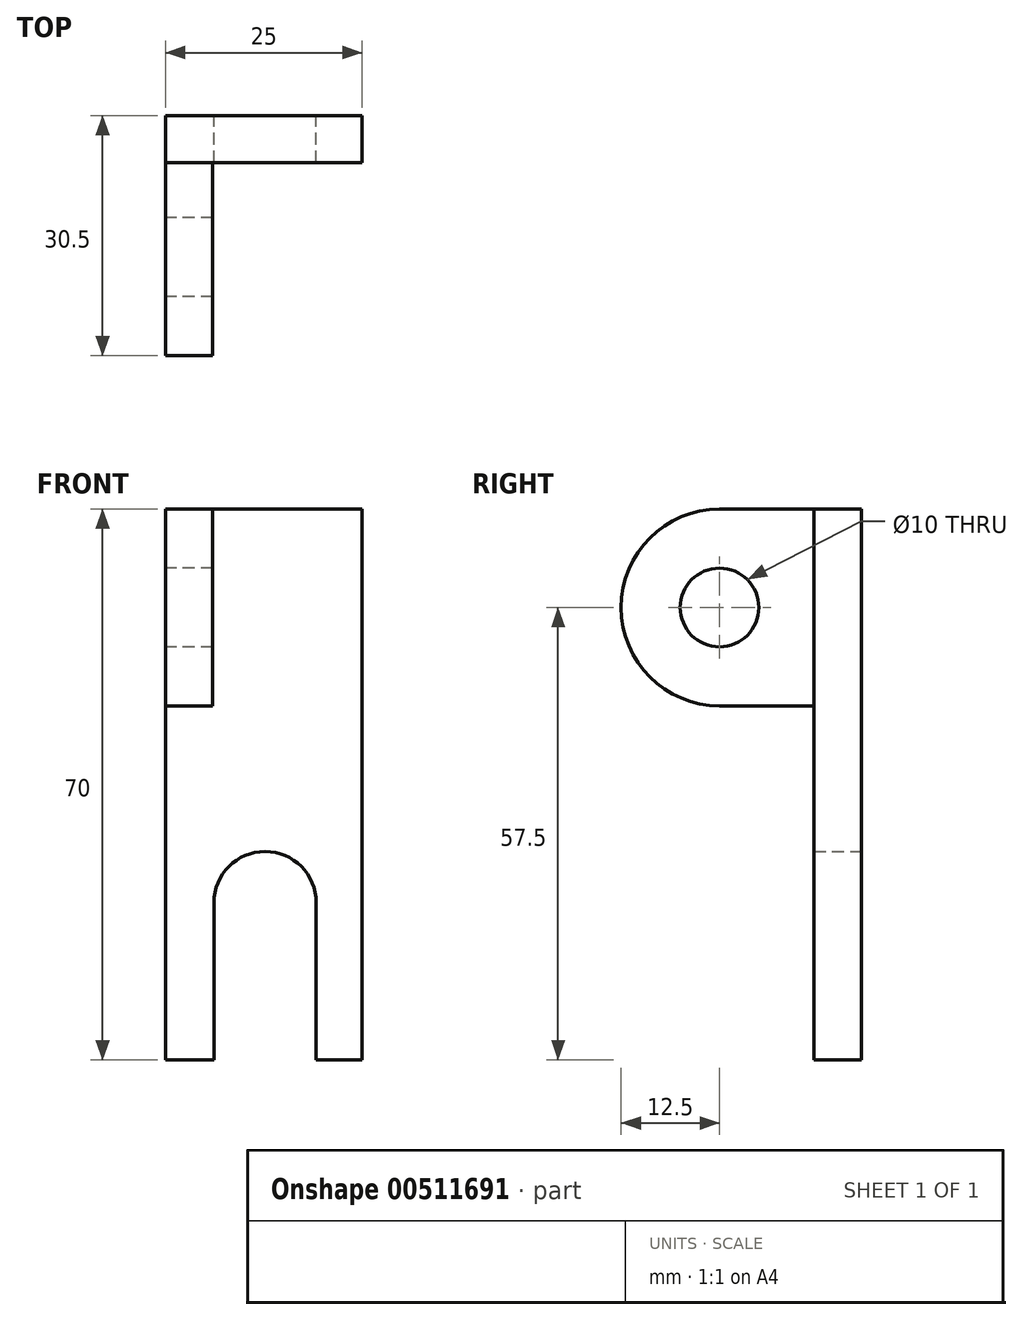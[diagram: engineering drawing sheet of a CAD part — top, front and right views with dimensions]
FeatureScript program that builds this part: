
annotation { "Feature Type Name" : "Feature", "Feature Type Description" : "" }
export const myFeature = defineFeature(function(context is Context, id is Id, definition is map)
    precondition{}
    {
        {
            var Q0;
            Q0=qCreatedBy(makeId("Front.planeOp"),FACE);
            var sketch = newSketch(context, id + "F0", { "sketchPlane" : qUnion([Q0])});
            skLineSegment(sketch, "E0.bottom", {"start": v(-12.5, 32) * mm, "end": v(12.5, 32) * mm});
            skLineSegment(sketch, "E0.top", {"start": v(-12.5, -32) * mm, "end": v(12.5, -32) * mm});
            skLineSegment(sketch, "E0.left", {"start": v(-12.5, 32) * mm, "end": v(-12.5, -32) * mm});
            skLineSegment(sketch, "E0.right", {"start": v(12.5, 32) * mm, "end": v(12.5, -32) * mm});
            skPoint(sketch, "E0.middle", {"position": v(0, 0) * mm});
            skSolve(sketch);
        }
        {
            var Q0;
            Q0 = qSketchRegion(id + "F0", true);
            extrude(context, id + "F1", {"entities" : qUnion([Q0]), "depth" : 6 * mm, "offsetDistance" : 25.4 * mm});
        }
        {
            var Q0;
            Q0=makeQuery(id+"F1.opExtrude","SWEPT_FACE",FACE,{"disambiguationData":[OSD([sQuery(id+"F0.wireOp",EDGE,"E0.bottom")])]});
            var sketch = newSketch(context, id + "F2", { "sketchPlane" : qUnion([Q0])});
            skLineSegment(sketch, "E1", {"start": v(-12.5, -6) * mm, "end": v(-12.5, 12) * mm});
            skLineSegment(sketch, "E2", {"start": v(12.5, -6) * mm, "end": v(12.5, 12) * mm});
            skArc(sketch, "E3", {"start": v(-12.5, 12) * mm, "mid": v(0, 24.5) * mm, "end": v(12.5, 12) * mm});
            skSolve(sketch);
        }
        {
            var Q0;
            {var subQ2=sQuery(id+"F2.wireOp",EDGE,"E3");Q0=makeQuery(id+"F2.imprint","IMPRINT",FACE,{"disambiguationData":[TD([[makeQuery(id+"F2.imprint","IMPRINT",EDGE,{"derivedFrom":subQ2}),-1.0]])]});}
            var Q1;
            {var subQ1=sQuery(id+"F0.wireOp",EDGE,"E0.bottom");var subQ2=makeQuery(id+"F1.opExtrude","CAP_EDGE",EDGE,{"disambiguationData":[OSD([subQ1])],"isStart":true});Q1=makeQuery(id+"F2.imprint","IMPRINT",FACE,{"disambiguationData":[TD([[makeQuery(id+"F2.imprint","IMPRINT",EDGE,{"derivedFrom":subQ2}),-1.0]])]});}
            extrude(context, id + "F3", {"entities" : qUnion([Q0, Q1]), "operationType" : NewBodyOperationType.ADD, "depth" : 6 * mm, "offsetDistance" : 25.4 * mm});
        }
        {
            var Q0;
            Q0=makeQuery(id+"F3.boolean.opBoolean","MERGE",FACE,{"derivedFrom":[makeQuery(id+"F1.opExtrude","SWEPT_FACE",FACE,{"disambiguationData":[OSD([sQuery(id+"F0.wireOp",EDGE,"E0.left")])]}),makeQuery(id+"F3.opExtrude","SWEPT_FACE",FACE,{"disambiguationData":[OSD([sQuery(id+"F2.wireOp",EDGE,"E1")])]})]});
            var sketch = newSketch(context, id + "F4", { "sketchPlane" : qUnion([Q0])});
            skPoint(sketch, "E4", {"position": v(0, 38) * mm});
            skPoint(sketch, "E5", {"position": v(0, 13) * mm});
            skLineSegment(sketch, "E6", {"start": v(0, 13) * mm, "end": v(18, 13) * mm});
            skLineSegment(sketch, "E7", {"start": v(0, 38) * mm, "end": v(18, 38) * mm});
            skArc(sketch, "E8", {"start": v(18, 13) * mm, "mid": v(30.5, 25.5) * mm, "end": v(18, 38) * mm});
            skSolve(sketch);
        }
        {
            var Q0;
            {var subQ0=sQuery(id+"F4.wireOp",EDGE,"E8");Q0=makeQuery(id+"F4.imprint","IMPRINT",FACE,{"disambiguationData":[TD([[makeQuery(id+"F4.imprint","IMPRINT",EDGE,{"derivedFrom":subQ0}),1.0]])]});}
            extrude(context, id + "F5", {"entities" : qUnion([Q0]), "oppositeDirection" : true, "depth" : 6 * mm, "offsetDistance" : 25.4 * mm});
        }
        {
            var Q0;
            Q0=makeQuery(id+"F3.opExtrude","CAP_FACE",FACE,{"disambiguationData":[OSD([sQuery(id+"F0.wireOp",EDGE,"E0.bottom"),sQuery(id+"F2.wireOp",EDGE,"E1"),sQuery(id+"F2.wireOp",EDGE,"E2"),sQuery(id+"F2.wireOp",EDGE,"E3")])],"isStart":false});
            var sketch = newSketch(context, id + "F6", { "sketchPlane" : qUnion([Q0])});
            skPoint(sketch, "E9", {"position": v(0, 12) * mm});
            skSolve(sketch);
        }
        {
            var Q0;
            Q0=sQuery(id+"F6.wireOp",VERTEX,"E9");
            var Q1;
            Q1=makeQuery(id+"F1.opExtrude","SWEPT_BODY",BODY,{"disambiguationData":[OSD([sQuery(id+"F0.wireOp",EDGE,"E0.bottom"),sQuery(id+"F0.wireOp",EDGE,"E0.top"),sQuery(id+"F0.wireOp",EDGE,"E0.left"),sQuery(id+"F0.wireOp",EDGE,"E0.right")])]});
            hole(context, id + "F7", {"style" : HoleStyle.SIMPLE, "endStyle" : HoleEndStyle.BLIND, "holeDiameter" : 10 * mm, "majorDiameter" : 6.35 * mm, "holeDepth" : 13 * mm, "isTappedThrough" : true, "tappedDepth" : 12.7 * mm, "tapClearance" : 3, "locations" : qUnion([Q0]), "scope" : qUnion([Q1])});
        }
        {
            var Q0;
            Q0=makeQuery(id+"F5.opExtrude","CAP_FACE",FACE,{"disambiguationData":[OSD([sQuery(id+"F0.wireOp",EDGE,"E0.bottom"),sQuery(id+"F0.wireOp",EDGE,"E0.left"),sQuery(id+"F2.wireOp",EDGE,"E1"),sQuery(id+"F4.wireOp",EDGE,"E6"),sQuery(id+"F4.wireOp",EDGE,"E7"),sQuery(id+"F4.wireOp",EDGE,"E8")])],"isStart":true});
            var sketch = newSketch(context, id + "F8", { "sketchPlane" : qUnion([Q0])});
            skPoint(sketch, "E10", {"position": v(18, 25.5) * mm});
            skSolve(sketch);
        }
        {
            var Q0;
            Q0=sQuery(id+"F8.wireOp",VERTEX,"E10");
            var Q1;
            Q1=makeQuery(id+"F5.opExtrude","SWEPT_BODY",BODY,{"disambiguationData":[OSD([sQuery(id+"F0.wireOp",EDGE,"E0.bottom"),sQuery(id+"F0.wireOp",EDGE,"E0.left"),sQuery(id+"F2.wireOp",EDGE,"E1"),sQuery(id+"F4.wireOp",EDGE,"E6"),sQuery(id+"F4.wireOp",EDGE,"E7"),sQuery(id+"F4.wireOp",EDGE,"E8")])]});
            hole(context, id + "F9", {"style" : HoleStyle.SIMPLE, "endStyle" : HoleEndStyle.BLIND, "holeDiameter" : 10 * mm, "majorDiameter" : 6.35 * mm, "holeDepth" : 13 * mm, "isTappedThrough" : true, "tappedDepth" : 12.7 * mm, "tapClearance" : 3, "locations" : qUnion([Q0]), "scope" : qUnion([Q1])});
        }
        {
            var Q0;
            Q0=makeQuery(id+"F1.opExtrude","CAP_FACE",FACE,{"disambiguationData":[OSD([sQuery(id+"F0.wireOp",EDGE,"E0.bottom"),sQuery(id+"F0.wireOp",EDGE,"E0.top"),sQuery(id+"F0.wireOp",EDGE,"E0.left"),sQuery(id+"F0.wireOp",EDGE,"E0.right")])],"isStart":true});
            var sketch = newSketch(context, id + "F10", { "sketchPlane" : qUnion([Q0])});
            skLineSegment(sketch, "E11", {"start": v(-6.66, -32) * mm, "end": v(-6.66, -12) * mm});
            skLineSegment(sketch, "E12", {"start": v(6.34, -32) * mm, "end": v(6.34, -12) * mm});
            skArc(sketch, "E13", {"start": v(-6.66, -12) * mm, "mid": v(-0.16, -5.5) * mm, "end": v(6.34, -12) * mm});
            skSolve(sketch);
        }
        {
            var Q0;
            {var subQ0=sQuery(id+"F10.wireOp",EDGE,"E11");Q0=makeQuery(id+"F10.imprint","IMPRINT",FACE,{"disambiguationData":[TD([[makeQuery(id+"F10.imprint","IMPRINT",EDGE,{"derivedFrom":subQ0}),-1.0]])]});}
            extrude(context, id + "F11", {"entities" : qUnion([Q0]), "operationType" : NewBodyOperationType.REMOVE, "oppositeDirection" : true, "depth" : 12.4 * mm, "offsetDistance" : 25 * mm});
        }
    });
